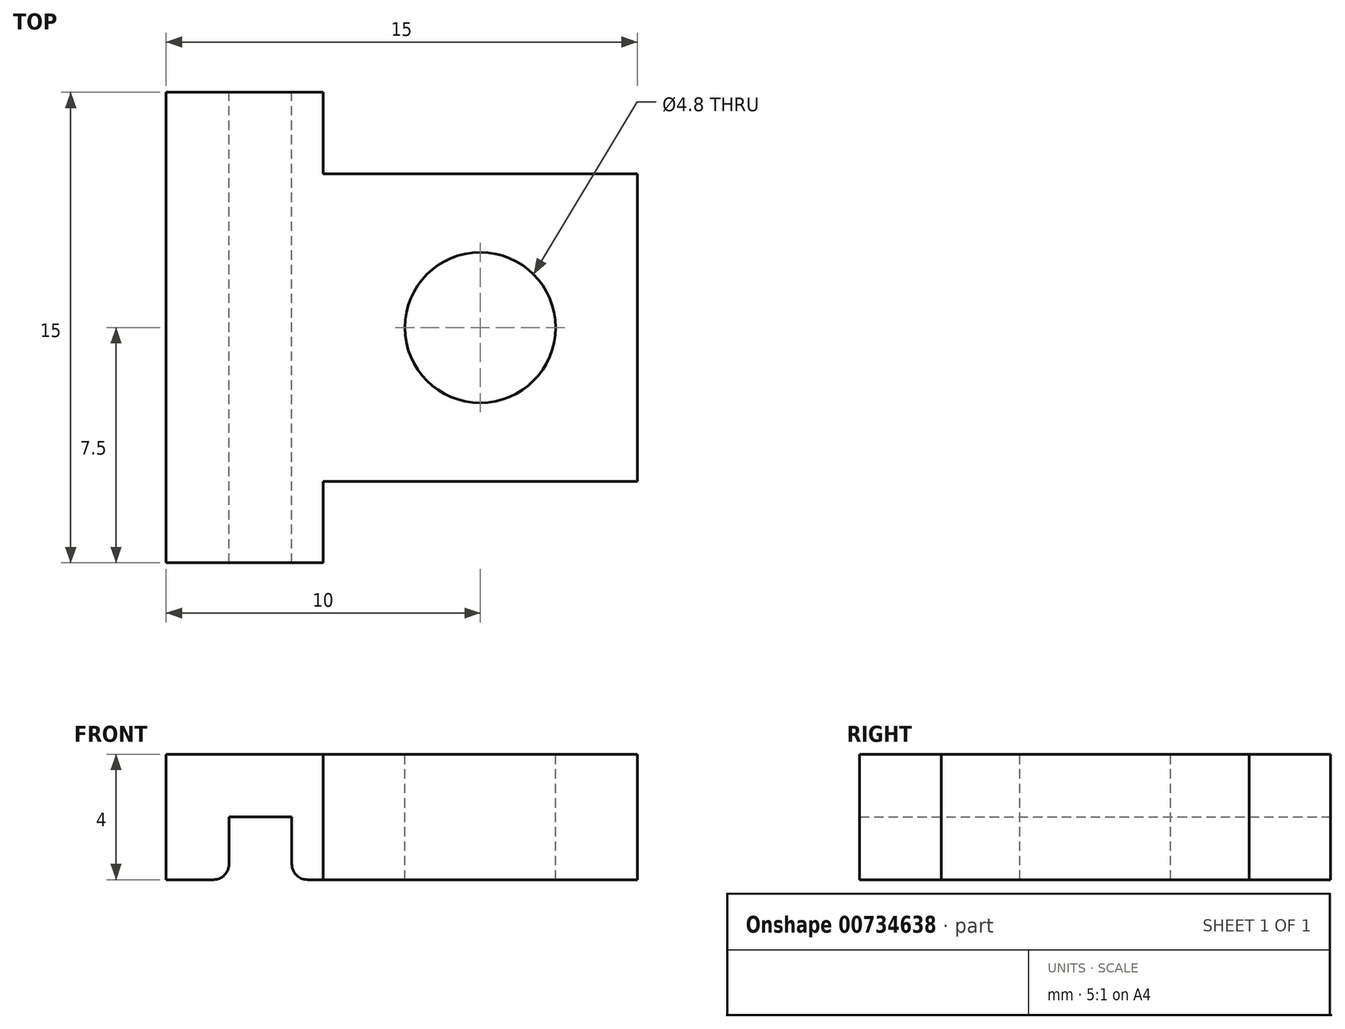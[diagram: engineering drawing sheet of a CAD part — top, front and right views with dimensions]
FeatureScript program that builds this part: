
annotation { "Feature Type Name" : "Feature", "Feature Type Description" : "" }
export const myFeature = defineFeature(function(context is Context, id is Id, definition is map)
    precondition{}
    {
        {
            var Q0;
            Q0=qCreatedBy(makeId("Front.planeOp"),FACE);
            var sketch = newSketch(context, id + "F0", { "sketchPlane" : qUnion([Q0])});
            skLineSegment(sketch, "E0.bottom", {"start": v(0, 0) * mm, "end": v(-11, 0) * mm});
            skLineSegment(sketch, "E0.top", {"start": v(0, 4) * mm, "end": v(-15, 4) * mm});
            skLineSegment(sketch, "E0.left", {"start": v(0, 0) * mm, "end": v(0, 4) * mm});
            skLineSegment(sketch, "E0.right", {"start": v(-15, 0) * mm, "end": v(-15, 4) * mm});
            skLineSegment(sketch, "E1.top", {"start": v(-13, 2) * mm, "end": v(-11, 2) * mm});
            skLineSegment(sketch, "E1.left", {"start": v(-13, 0) * mm, "end": v(-13, 2) * mm});
            skLineSegment(sketch, "E1.right", {"start": v(-11, 0) * mm, "end": v(-11, 2) * mm});
            skLineSegment(sketch, "E2.trimOffspring", {"start": v(-13, 0) * mm, "end": v(-15, 0) * mm});
            skSolve(sketch);
        }
        {
            var Q0;
            Q0 = qSketchRegion(id + "F0", true);
            extrude(context, id + "F1", {"entities" : qUnion([Q0]), "depth" : 7.5 * mm, "offsetDistance" : 25 * mm, "hasSecondDirection" : true, "secondDirectionOppositeDirection" : true, "secondDirectionDepth" : 7.5 * mm});
        }
        {
            var Q0;
            Q0=makeQuery(id+"F1.opExtrude","SWEPT_FACE",FACE,{"disambiguationData":[OSD([sQuery(id+"F0.wireOp",EDGE,"E0.top")])]});
            var sketch = newSketch(context, id + "F2", { "sketchPlane" : qUnion([Q0])});
            skCircle(sketch, "E3", {"center": v(-5, 0) * mm, "radius": 2.4 * mm});
            skSolve(sketch);
        }
        {
            var Q0;
            Q0 = qSketchRegion(id + "F2", true);
            extrude(context, id + "F3", {"entities" : qUnion([Q0]), "operationType" : NewBodyOperationType.REMOVE, "endBound" : BoundingType.THROUGH_ALL, "oppositeDirection" : true, "depth" : 25 * mm, "offsetDistance" : 25 * mm});
        }
        {
            var Q0;
            Q0=makeQuery(id+"F1.opExtrude","SWEPT_FACE",FACE,{"disambiguationData":[OSD([sQuery(id+"F0.wireOp",EDGE,"E0.top")])]});
            var sketch = newSketch(context, id + "F4", { "sketchPlane" : qUnion([Q0])});
            skLineSegment(sketch, "E4.bottom", {"start": v(0, 7.5) * mm, "end": v(-10, 7.5) * mm});
            skLineSegment(sketch, "E4.top", {"start": v(0, 4.9) * mm, "end": v(-10, 4.9) * mm});
            skLineSegment(sketch, "E4.left", {"start": v(0, 7.5) * mm, "end": v(0, 4.9) * mm});
            skLineSegment(sketch, "E4.right", {"start": v(-10, 7.5) * mm, "end": v(-10, 4.9) * mm});
            skLineSegment(sketch, "E5.MirrorCS", {"start": v(0, -7.5) * mm, "end": v(0, -4.9) * mm});
            skLineSegment(sketch, "E6.MirrorCS", {"start": v(0, -7.5) * mm, "end": v(-10, -7.5) * mm});
            skLineSegment(sketch, "E7.MirrorCS", {"start": v(-10, -7.5) * mm, "end": v(-10, -4.9) * mm});
            skLineSegment(sketch, "E8.MirrorCS", {"start": v(0, -4.9) * mm, "end": v(-10, -4.9) * mm});
            skSolve(sketch);
        }
        {
            var Q0;
            Q0 = qSketchRegion(id + "F4", true);
            extrude(context, id + "F5", {"entities" : qUnion([Q0]), "operationType" : NewBodyOperationType.REMOVE, "endBound" : BoundingType.THROUGH_ALL, "oppositeDirection" : true, "depth" : 25 * mm, "offsetDistance" : 25 * mm});
        }
        {
            var Q0;
            Q0=makeQuery(id+"F1.opExtrude","SWEPT_EDGE",EDGE,{"disambiguationData":[OSD([sQuery(id+"F0.wireOp",EDGE,"E1.left"),sQuery(id+"F0.wireOp",EDGE,"E2.trimOffspring")])]});
            var Q1;
            Q1=makeQuery(id+"F1.opExtrude","SWEPT_EDGE",EDGE,{"disambiguationData":[OSD([sQuery(id+"F0.wireOp",EDGE,"E0.bottom"),sQuery(id+"F0.wireOp",EDGE,"E1.right")])]});
            fillet(context, id + "F6", {"entities" : qUnion([Q0, Q1]), "tangentPropagation" : true, "radius" : 0.5 * mm, "defaultsChanged" : false, "vertexSettings" : [], "allowEdgeOverflow" : false});
        }
    });
